# Revit family: Kühlschrank-Normalkühlung Standard 570L-Magnos - Zentral
name_source: partatom
category: Sonderausstattung
revit_build: Autodesk Revit 2015 (Build: 20140606_1530(x64)
units: mm (PartAtom-declared; Revit-internal decimal feet)

## types (1)
- BR 570 - 720 x 840 x 2050
    Artikelnr. = HKON057-MS
    Breite = 720 mm  [stored 2.3622 ft]
    DN Flüssigkeitsleitung = 6 mm  [stored 0.019685 ft]
    DN Saugleitung = 8 mm  [stored 0.0262467 ft]
    DN Tauwasserabfluß = 12 mm  [stored 0.0393701 ft]
    Dichtung Stärke = 14 mm  [stored 0.0459318 ft]
    Elektroanschluss Abstand Seite = 250 mm  [stored 0.82021 ft]
    Elektroanschluss Höhe = 1800 mm  [stored 5.90551 ft]
    Energieeffizienzklasse = B
    Flüssigkeitsleitung Abstand Seite = 150 mm  [stored 0.492126 ft]
    Flüssigkeitsleitung Höhe = 1800 mm  [stored 5.90551 ft]
    Füße Abstand Hinten = 82 mm  [stored 0.269029 ft]
    Füße Abstand Seiten = 90 mm  [stored 0.295276 ft]
    Füße Abstand Vorne = 50 mm  [stored 0.164042 ft]
    Hersteller = CoolCompact
    Kapazität = 23 x GN2/1
    Kopfteil Höhe = 337 mm  [stored 1.10564 ft]
    Kopfteil Tiefe = 70 mm  [stored 0.229659 ft]
    Kopfteil Verlängerung = 25 mm  [stored 0.082021 ft]
    Korpus Höhe = 1563 mm  [stored 5.12795 ft]
    Korpus Tiefe = 770 mm  [stored 2.52625 ft]
    Kälteleistung = 340W bei -10°C VT/+32°C UT
    Kältemittel = R290
    Material = Edelstahl AISI 304
    Netzkabellänge = 2500 mm  [stored 8.2021 ft]
    Pole = 1
    Saugleitung Abstand Seite = 200 mm  [stored 0.656168 ft]
    Saugleitung Höhe = 1800 mm  [stored 5.90551 ft]
    Scheinleistung = 0 VA
    Sockelhöhe = 150 mm  [stored 0.492126 ft]
    Spannung = 230 V
    Tauwasserabfluss Abstand Seite = 360 mm  [stored 1.1811 ft]
    Tauwasserabfluss Höhe = 1720 mm  [stored 5.64304 ft]
    Temp. Bereich = -2°C / +12°C
    Türabstand Links = 5 mm  [stored 0.0164042 ft]
    Türabstand Oben = 6 mm  [stored 0.019685 ft]
    Türabstand Rechts = 5 mm  [stored 0.0164042 ft]
    Türabstand Unten = 58 mm  [stored 0.190289 ft]
    Türen Anzahl = 1
    Türen Breite = 710 mm
    Türen Höhe = 1474 mm  [stored 4.83596 ft]
    Türen Stärke = 56 mm  [stored 0.183727 ft]
    Wandstärke Hinten = 65 mm  [stored 0.213255 ft]
    Wandstärke Oben = 95 mm
    Wandstärke Seiten = 93 mm  [stored 0.305118 ft]
    Wandstärke Unten = 90 mm  [stored 0.295276 ft]
    Watt = 150 W

note: [stored X ft] marks values corroborated as IEEE doubles in the binary element streams (Revit-internal decimal feet)

## geometry (parser evidence)
native form markers: Blend x30, Sweep x3
no freeform markers — native parametric forms only
